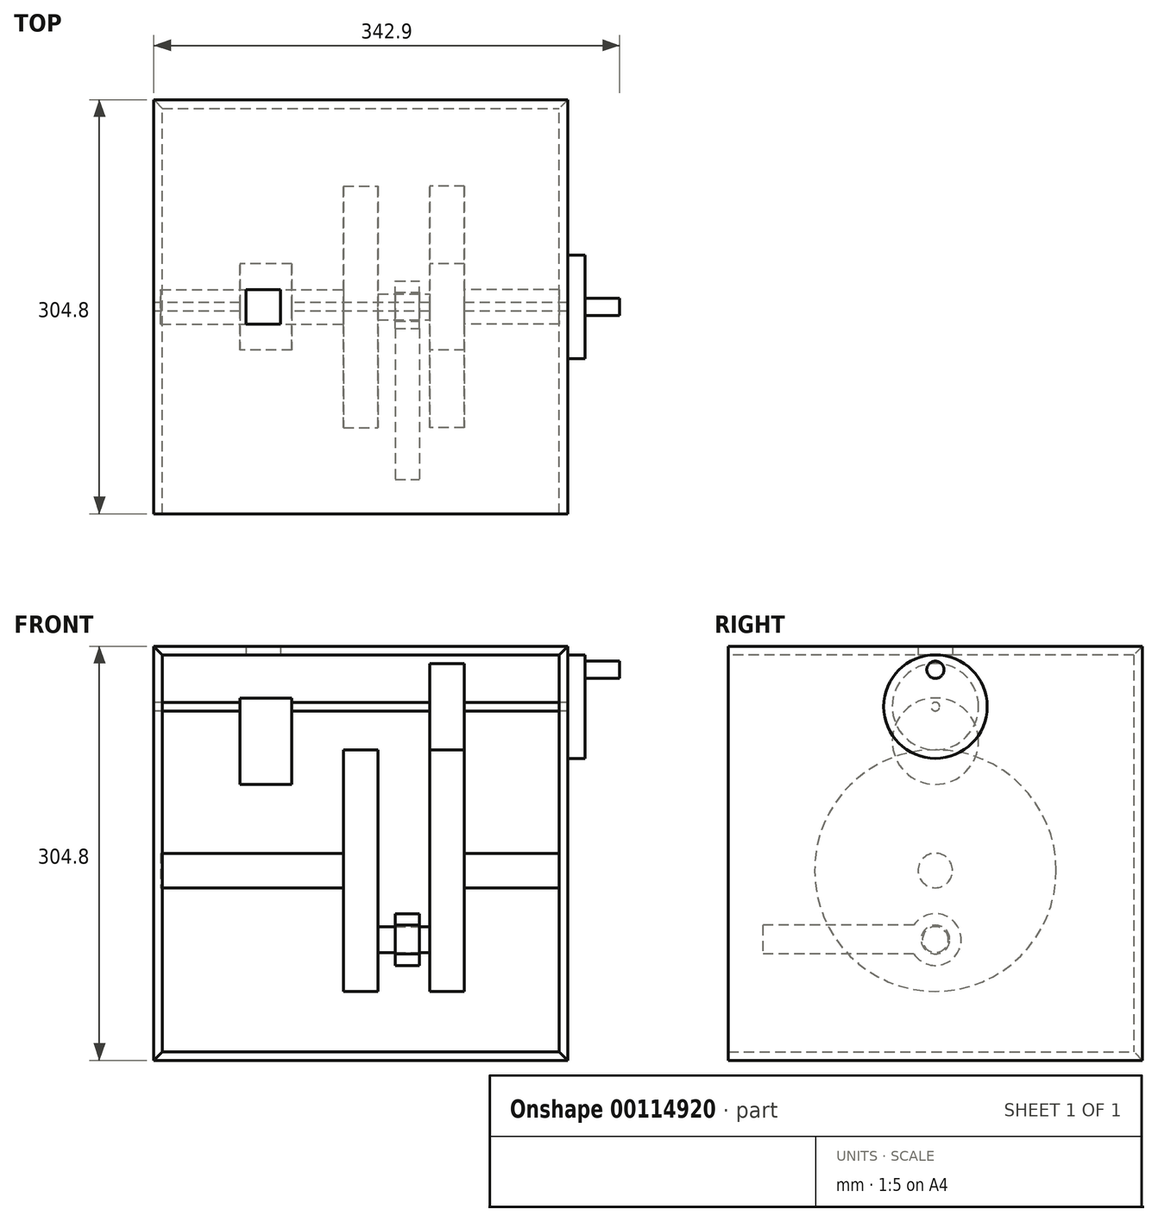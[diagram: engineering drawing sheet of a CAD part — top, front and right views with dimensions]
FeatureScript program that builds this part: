
annotation { "Feature Type Name" : "Feature", "Feature Type Description" : "" }
export const myFeature = defineFeature(function(context is Context, id is Id, definition is map)
    precondition{}
    {
        {
            var Q0;
            Q0=qCreatedBy(makeId("Right.planeOp"),FACE);
            var sketch = newSketch(context, id + "F0", { "sketchPlane" : qUnion([Q0])});
            skCircle(sketch, "E0", {"center": v(0, 0) * mm, "radius": 3.18 * mm});
            skSolve(sketch);
        }
        {
            var Q0;
            Q0=makeQuery(id+"F0.imprint","IMPRINT",FACE,{"disambiguationData":[TD([[makeQuery(id+"F0.imprint","IMPRINT",EDGE,{"derivedFrom":sQuery(id+"F0.wireOp",EDGE,"E0")}),1.0]])]});
            extrude(context, id + "F1", {"entities" : qUnion([Q0]), "depth" : 304.8 * mm});
        }
        {
            var Q0;
            Q0=qCreatedBy(makeId("Right.planeOp"),FACE);
            cPlane(context, id + "F2", {"entities" : qUnion([Q0]), "cplaneType" : CPlaneType.OFFSET, "offset" : 63.5 * mm, "width" : 152.4 * mm, "height" : 152.4 * mm});
        }
        {
            var Q0;
            Q0=qCreatedBy(id+"F2.planeOp",FACE);
            var sketch = newSketch(context, id + "F3", { "sketchPlane" : qUnion([Q0])});
            skCircle(sketch, "E1", {"center": v(0, -25.4) * mm, "radius": 31.75 * mm});
            skSolve(sketch);
        }
        {
            var Q0;
            Q0=makeQuery(id+"F3.imprint","IMPRINT",FACE,{"disambiguationData":[TD([[makeQuery(id+"F3.imprint","IMPRINT",EDGE,{"derivedFrom":sQuery(id+"F3.wireOp",EDGE,"E1")}),1.0]])]});
            extrude(context, id + "F4", {"entities" : qUnion([Q0]), "operationType" : NewBodyOperationType.ADD, "depth" : 38.1 * mm});
        }
        {
            var Q0;
            Q0=qCreatedBy(makeId("Top.planeOp"),FACE);
            cPlane(context, id + "F5", {"entities" : qUnion([Q0]), "cplaneType" : CPlaneType.OFFSET, "offset" : 38.1 * mm, "width" : 152.4 * mm, "height" : 152.4 * mm});
        }
        {
            var Q0;
            Q0=qCreatedBy(id+"F5.planeOp",FACE);
            var sketch = newSketch(context, id + "F6", { "sketchPlane" : qUnion([Q0])});
            skLineSegment(sketch, "E2.bottom", {"start": v(0, -152.4) * mm, "end": v(304.8, -152.4) * mm});
            skLineSegment(sketch, "E2.top", {"start": v(0, 152.4) * mm, "end": v(304.8, 152.4) * mm});
            skLineSegment(sketch, "E2.left", {"start": v(0, -152.4) * mm, "end": v(0, 152.4) * mm});
            skLineSegment(sketch, "E2.right", {"start": v(304.8, -152.4) * mm, "end": v(304.8, 152.4) * mm});
            skLineSegment(sketch, "E3.bottom", {"start": v(93.2, 12.7) * mm, "end": v(67.8, 12.7) * mm});
            skLineSegment(sketch, "E3.top", {"start": v(93.2, -12.7) * mm, "end": v(67.8, -12.7) * mm});
            skLineSegment(sketch, "E3.left", {"start": v(93.2, 12.7) * mm, "end": v(93.2, -12.7) * mm});
            skLineSegment(sketch, "E3.right", {"start": v(67.8, 12.7) * mm, "end": v(67.8, -12.7) * mm});
            skPoint(sketch, "E3.middle", {"position": v(80.5, 0) * mm});
            skSolve(sketch);
        }
        {
            var Q0;
            Q0=makeQuery(id+"F6.imprint","IMPRINT",FACE,{"disambiguationData":[TD([[makeQuery(id+"F6.imprint","IMPRINT",EDGE,{"derivedFrom":sQuery(id+"F6.wireOp",EDGE,"E2.bottom")}),1.0]])]});
            extrude(context, id + "F7", {"entities" : qUnion([Q0]), "depth" : 6.35 * mm});
        }
        {
            var Q0;
            Q0=makeQuery(id+"F7.opExtrude","CAP_EDGE",EDGE,{"disambiguationData":[OSD([sQuery(id+"F6.wireOp",EDGE,"E2.right")])],"isStart":true});
            var Q1;
            Q1=makeQuery(id+"F7.opExtrude","CAP_EDGE",EDGE,{"disambiguationData":[OSD([sQuery(id+"F6.wireOp",EDGE,"E2.top")])],"isStart":true});
            var Q2;
            Q2=makeQuery(id+"F7.opExtrude","CAP_EDGE",EDGE,{"disambiguationData":[OSD([sQuery(id+"F6.wireOp",EDGE,"E2.left")])],"isStart":true});
            chamfer(context, id + "F8", {"entities" : qUnion([Q0, Q1, Q2]), "width" : 6.35 * mm, "tangentPropagation" : true});
        }
        {
            var Q0;
            Q0=qCreatedBy(makeId("Right.planeOp"),FACE);
            var sketch = newSketch(context, id + "F9", { "sketchPlane" : qUnion([Q0])});
            skLineSegment(sketch, "E4.bottom", {"start": v(-152.4, -260.35) * mm, "end": v(152.4, -260.35) * mm});
            skLineSegment(sketch, "E4.top", {"start": v(-152.4, 44.45) * mm, "end": v(152.4, 44.45) * mm});
            skLineSegment(sketch, "E4.left", {"start": v(-152.4, -260.35) * mm, "end": v(-152.4, 44.45) * mm});
            skLineSegment(sketch, "E4.right", {"start": v(152.4, -260.35) * mm, "end": v(152.4, 44.45) * mm});
            skSolve(sketch);
        }
        {
            var Q0;
            Q0 = qSketchRegion(id + "F9", true);
            extrude(context, id + "F10", {"entities" : qUnion([Q0]), "depth" : 6.35 * mm});
        }
        {
            var Q0;
            Q0=makeQuery(id+"F10.opExtrude","CAP_EDGE",EDGE,{"disambiguationData":[OSD([sQuery(id+"F9.wireOp",EDGE,"E4.top")])],"isStart":false});
            var Q1;
            Q1=makeQuery(id+"F10.opExtrude","CAP_EDGE",EDGE,{"disambiguationData":[OSD([sQuery(id+"F9.wireOp",EDGE,"E4.bottom")])],"isStart":false});
            var Q2;
            Q2=makeQuery(id+"F10.opExtrude","CAP_EDGE",EDGE,{"disambiguationData":[OSD([sQuery(id+"F9.wireOp",EDGE,"E4.right")])],"isStart":false});
            chamfer(context, id + "F11", {"entities" : qUnion([Q0, Q1, Q2]), "width" : 6.35 * mm, "tangentPropagation" : true});
        }
        {
            var Q0;
            Q0=qCreatedBy(makeId("Front.planeOp"),FACE);
            cPlane(context, id + "F12", {"entities" : qUnion([Q0]), "cplaneType" : CPlaneType.OFFSET, "offset" : 152.4 * mm, "oppositeDirection" : true, "width" : 152.4 * mm, "height" : 152.4 * mm});
        }
        {
            var Q0;
            Q0=qCreatedBy(id+"F12.planeOp",FACE);
            var sketch = newSketch(context, id + "F13", { "sketchPlane" : qUnion([Q0])});
            skLineSegment(sketch, "E5.bottom", {"start": v(0, 44.45) * mm, "end": v(304.8, 44.45) * mm});
            skLineSegment(sketch, "E5.top", {"start": v(0, -260.35) * mm, "end": v(304.8, -260.35) * mm});
            skLineSegment(sketch, "E5.left", {"start": v(0, 44.45) * mm, "end": v(0, -260.35) * mm});
            skLineSegment(sketch, "E5.right", {"start": v(304.8, 44.45) * mm, "end": v(304.8, -260.35) * mm});
            skSolve(sketch);
        }
        {
            var Q0;
            Q0=makeQuery(id+"F13.imprint","IMPRINT",FACE,{"disambiguationData":[TD([[makeQuery(id+"F13.imprint","IMPRINT",EDGE,{"derivedFrom":sQuery(id+"F13.wireOp",EDGE,"E5.bottom")}),-1.0]])]});
            extrude(context, id + "F14", {"entities" : qUnion([Q0]), "depth" : 6.35 * mm});
        }
        {
            var Q0;
            Q0=makeQuery(id+"F14.opExtrude","CAP_EDGE",EDGE,{"disambiguationData":[OSD([sQuery(id+"F13.wireOp",EDGE,"E5.bottom")])],"isStart":false});
            var Q1;
            Q1=makeQuery(id+"F14.opExtrude","CAP_EDGE",EDGE,{"disambiguationData":[OSD([sQuery(id+"F13.wireOp",EDGE,"E5.right")])],"isStart":false});
            var Q2;
            Q2=makeQuery(id+"F14.opExtrude","CAP_EDGE",EDGE,{"disambiguationData":[OSD([sQuery(id+"F13.wireOp",EDGE,"E5.top")])],"isStart":false});
            var Q3;
            Q3=makeQuery(id+"F14.opExtrude","CAP_EDGE",EDGE,{"disambiguationData":[OSD([sQuery(id+"F13.wireOp",EDGE,"E5.left")])],"isStart":false});
            chamfer(context, id + "F15", {"entities" : qUnion([Q0, Q1, Q2, Q3]), "width" : 6.35 * mm, "tangentPropagation" : true});
        }
        {
            var Q0;
            Q0=makeQuery(id+"F7.opExtrude","CAP_FACE",FACE,{"disambiguationData":[OSD([sQuery(id+"F6.wireOp",EDGE,"E2.bottom"),sQuery(id+"F6.wireOp",EDGE,"E2.top"),sQuery(id+"F6.wireOp",EDGE,"E2.left"),sQuery(id+"F6.wireOp",EDGE,"E2.right"),sQuery(id+"F6.wireOp",EDGE,"E3.bottom"),sQuery(id+"F6.wireOp",EDGE,"E3.top"),sQuery(id+"F6.wireOp",EDGE,"E3.left"),sQuery(id+"F6.wireOp",EDGE,"E3.right")])],"isStart":false});
            cPlane(context, id + "F16", {"entities" : qUnion([Q0]), "cplaneType" : CPlaneType.OFFSET, "offset" : 304.8 * mm, "oppositeDirection" : true, "width" : 152.4 * mm, "height" : 152.4 * mm});
        }
        {
            var Q0;
            Q0=qCreatedBy(id+"F16.planeOp",FACE);
            var sketch = newSketch(context, id + "F17", { "sketchPlane" : qUnion([Q0])});
            skLineSegment(sketch, "E6.bottom", {"start": v(0, 152.4) * mm, "end": v(304.8, 152.4) * mm});
            skLineSegment(sketch, "E6.top", {"start": v(0, -152.4) * mm, "end": v(304.8, -152.4) * mm});
            skLineSegment(sketch, "E6.left", {"start": v(0, 152.4) * mm, "end": v(0, -152.4) * mm});
            skLineSegment(sketch, "E6.right", {"start": v(304.8, 152.4) * mm, "end": v(304.8, -152.4) * mm});
            skSolve(sketch);
        }
        {
            var Q0;
            Q0=makeQuery(id+"F17.imprint","IMPRINT",FACE,{"disambiguationData":[TD([[makeQuery(id+"F17.imprint","IMPRINT",EDGE,{"derivedFrom":sQuery(id+"F17.wireOp",EDGE,"E6.bottom")}),-1.0]])]});
            extrude(context, id + "F18", {"entities" : qUnion([Q0]), "depth" : 6.35 * mm});
        }
        {
            var Q0;
            Q0=makeQuery(id+"F18.opExtrude","CAP_EDGE",EDGE,{"disambiguationData":[OSD([sQuery(id+"F17.wireOp",EDGE,"E6.left")])],"isStart":false});
            var Q1;
            Q1=makeQuery(id+"F18.opExtrude","CAP_EDGE",EDGE,{"disambiguationData":[OSD([sQuery(id+"F17.wireOp",EDGE,"E6.bottom")])],"isStart":false});
            var Q2;
            Q2=makeQuery(id+"F18.opExtrude","CAP_EDGE",EDGE,{"disambiguationData":[OSD([sQuery(id+"F17.wireOp",EDGE,"E6.right")])],"isStart":false});
            chamfer(context, id + "F19", {"entities" : qUnion([Q0, Q1, Q2]), "width" : 6.35 * mm, "tangentPropagation" : true});
        }
        {
            var Q0;
            Q0=qCreatedBy(makeId("Right.planeOp"),FACE);
            cPlane(context, id + "F20", {"entities" : qUnion([Q0]), "cplaneType" : CPlaneType.OFFSET, "offset" : 203.2 * mm, "width" : 152.4 * mm, "height" : 152.4 * mm});
        }
        {
            var Q0;
            Q0=qCreatedBy(id+"F20.planeOp",FACE);
            var sketch = newSketch(context, id + "F21", { "sketchPlane" : qUnion([Q0])});
            skCircle(sketch, "E7", {"center": v(0, 0) * mm, "radius": 31.75 * mm});
            skCircle(sketch, "E8", {"center": v(0, -120.65) * mm, "radius": 88.9 * mm});
            skSolve(sketch);
        }
        {
            var Q0;
            Q0=makeQuery(id+"F21.imprint","IMPRINT",FACE,{"disambiguationData":[TD([[makeQuery(id+"F21.imprint","IMPRINT",EDGE,{"derivedFrom":sQuery(id+"F21.wireOp",EDGE,"E8")}),1.0]])]});
            var Q1;
            Q1=makeQuery(id+"F21.imprint","IMPRINT",FACE,{"disambiguationData":[TD([[makeQuery(id+"F21.imprint","IMPRINT",EDGE,{"derivedFrom":sQuery(id+"F21.wireOp",EDGE,"E7")}),1.0]])]});
            extrude(context, id + "F22", {"entities" : qUnion([Q0, Q1]), "operationType" : NewBodyOperationType.ADD, "depth" : 25.4 * mm});
        }
        {
            var Q0;
            Q0=makeQuery(id+"F22.opExtrude","CAP_FACE",FACE,{"disambiguationData":[OSD([sQuery(id+"F21.wireOp",EDGE,"E8")])],"isStart":true});
            var sketch = newSketch(context, id + "F23", { "sketchPlane" : qUnion([Q0])});
            skCircle(sketch, "E9", {"center": v(0, -171.45) * mm, "radius": 9.53 * mm});
            skSolve(sketch);
        }
        {
            var Q0;
            Q0=makeQuery(id+"F23.imprint","IMPRINT",FACE,{"disambiguationData":[TD([[makeQuery(id+"F23.imprint","IMPRINT",EDGE,{"derivedFrom":sQuery(id+"F23.wireOp",EDGE,"E9")}),1.0]])]});
            var Q1;
            Q1=sQuery(id+"F23.wireOp",EDGE,"E9");
            extrude(context, id + "F24", {"entities" : qUnion([Q0]), "surfaceEntities" : qUnion([Q1]), "depth" : 38.1 * mm});
        }
        {
            var Q0;
            Q0=qCreatedBy(makeId("Right.planeOp"),FACE);
            cPlane(context, id + "F25", {"entities" : qUnion([Q0]), "cplaneType" : CPlaneType.OFFSET, "offset" : 304.8 * mm, "width" : 152.4 * mm, "height" : 152.4 * mm});
        }
        {
            var Q0;
            Q0=qCreatedBy(id+"F25.planeOp",FACE);
            var sketch = newSketch(context, id + "F26", { "sketchPlane" : qUnion([Q0])});
            skLineSegment(sketch, "E10.bottom", {"start": v(152.4, 44.45) * mm, "end": v(-152.4, 44.45) * mm});
            skLineSegment(sketch, "E10.top", {"start": v(152.4, -260.35) * mm, "end": v(-152.4, -260.35) * mm});
            skLineSegment(sketch, "E10.left", {"start": v(152.4, 44.45) * mm, "end": v(152.4, -260.35) * mm});
            skLineSegment(sketch, "E10.right", {"start": v(-152.4, 44.45) * mm, "end": v(-152.4, -260.35) * mm});
            skSolve(sketch);
        }
        {
            var Q0;
            Q0=makeQuery(id+"F26.imprint","IMPRINT",FACE,{"disambiguationData":[TD([[makeQuery(id+"F26.imprint","IMPRINT",EDGE,{"derivedFrom":sQuery(id+"F26.wireOp",EDGE,"E10.bottom")}),1.0]])]});
            extrude(context, id + "F27", {"entities" : qUnion([Q0]), "oppositeDirection" : true, "depth" : 6.35 * mm});
        }
        {
            var Q0;
            Q0=makeQuery(id+"F27.opExtrude","CAP_EDGE",EDGE,{"disambiguationData":[OSD([sQuery(id+"F26.wireOp",EDGE,"E10.bottom")])],"isStart":false});
            var Q1;
            Q1=makeQuery(id+"F27.opExtrude","CAP_EDGE",EDGE,{"disambiguationData":[OSD([sQuery(id+"F26.wireOp",EDGE,"E10.left")])],"isStart":false});
            var Q2;
            Q2=makeQuery(id+"F27.opExtrude","CAP_EDGE",EDGE,{"disambiguationData":[OSD([sQuery(id+"F26.wireOp",EDGE,"E10.top")])],"isStart":false});
            chamfer(context, id + "F28", {"entities" : qUnion([Q0, Q1, Q2]), "width" : 6.35 * mm, "tangentPropagation" : true});
        }
        {
            var Q0;
            Q0=makeQuery(id+"F27.opExtrude","CAP_FACE",FACE,{"disambiguationData":[OSD([sQuery(id+"F26.wireOp",EDGE,"E10.bottom"),sQuery(id+"F26.wireOp",EDGE,"E10.top"),sQuery(id+"F26.wireOp",EDGE,"E10.left"),sQuery(id+"F26.wireOp",EDGE,"E10.right")])],"isStart":true});
            var sketch = newSketch(context, id + "F29", { "sketchPlane" : qUnion([Q0])});
            skCircle(sketch, "E11", {"center": v(0, 0) * mm, "radius": 38.1 * mm});
            skSolve(sketch);
        }
        {
            var Q0;
            Q0 = qSketchRegion(id + "F29", true);
            extrude(context, id + "F30", {"entities" : qUnion([Q0]), "depth" : 12.7 * mm});
        }
        {
            var Q0;
            Q0=makeQuery(id+"F30.opExtrude","CAP_FACE",FACE,{"disambiguationData":[OSD([sQuery(id+"F29.wireOp",EDGE,"E11")])],"isStart":false});
            var sketch = newSketch(context, id + "F31", { "sketchPlane" : qUnion([Q0])});
            skCircle(sketch, "E12", {"center": v(0, 27.1) * mm, "radius": 6.35 * mm});
            skSolve(sketch);
        }
        {
            var Q0;
            Q0=makeQuery(id+"F31.imprint","IMPRINT",FACE,{"disambiguationData":[TD([[makeQuery(id+"F31.imprint","IMPRINT",EDGE,{"derivedFrom":sQuery(id+"F31.wireOp",EDGE,"E12")}),1.0]])]});
            extrude(context, id + "F32", {"entities" : qUnion([Q0]), "operationType" : NewBodyOperationType.ADD, "depth" : 25.4 * mm});
        }
        {
            var Q0;
            Q0=makeQuery(id+"F22.opExtrude","CAP_FACE",FACE,{"disambiguationData":[OSD([sQuery(id+"F21.wireOp",EDGE,"E8")])],"isStart":false});
            var sketch = newSketch(context, id + "F33", { "sketchPlane" : qUnion([Q0])});
            skCircle(sketch, "E13", {"center": v(0, -120.65) * mm, "radius": 12.7 * mm});
            skSolve(sketch);
        }
        {
            var Q0;
            Q0=makeQuery(id+"F33.imprint","IMPRINT",FACE,{"disambiguationData":[TD([[makeQuery(id+"F33.imprint","IMPRINT",EDGE,{"derivedFrom":sQuery(id+"F33.wireOp",EDGE,"E13")}),1.0]])]});
            var Q1;
            Q1=sQuery(id+"F33.wireOp",EDGE,"E13");
            extrude(context, id + "F34", {"entities" : qUnion([Q0]), "surfaceEntities" : qUnion([Q1]), "depth" : 69.85 * mm});
        }
        {
            var Q0;
            Q0=makeQuery(id+"F22.opExtrude","CAP_FACE",FACE,{"disambiguationData":[OSD([sQuery(id+"F21.wireOp",EDGE,"E8")])],"isStart":true});
            cPlane(context, id + "F35", {"entities" : qUnion([Q0]), "cplaneType" : CPlaneType.OFFSET, "offset" : 38.1 * mm, "width" : 152.4 * mm, "height" : 152.4 * mm});
        }
        {
            var Q0;
            Q0=qCreatedBy(id+"F35.planeOp",FACE);
            var sketch = newSketch(context, id + "F36", { "sketchPlane" : qUnion([Q0])});
            skCircle(sketch, "E14", {"center": v(0, -120.65) * mm, "radius": 88.9 * mm});
            skSolve(sketch);
        }
        {
            var Q0;
            Q0=makeQuery(id+"F36.imprint","IMPRINT",FACE,{"disambiguationData":[TD([[makeQuery(id+"F36.imprint","IMPRINT",EDGE,{"derivedFrom":sQuery(id+"F36.wireOp",EDGE,"E14")}),1.0]])]});
            extrude(context, id + "F37", {"entities" : qUnion([Q0]), "operationType" : NewBodyOperationType.ADD, "depth" : 25.4 * mm});
        }
        {
            var Q0;
            Q0=makeQuery(id+"F37.opExtrude","CAP_FACE",FACE,{"disambiguationData":[OSD([sQuery(id+"F36.wireOp",EDGE,"E14")])],"isStart":false});
            var sketch = newSketch(context, id + "F38", { "sketchPlane" : qUnion([Q0])});
            skCircle(sketch, "E15", {"center": v(0, -120.65) * mm, "radius": 12.7 * mm});
            skSolve(sketch);
        }
        {
            var Q0;
            Q0=makeQuery(id+"F38.imprint","IMPRINT",FACE,{"disambiguationData":[TD([[makeQuery(id+"F38.imprint","IMPRINT",EDGE,{"derivedFrom":sQuery(id+"F38.wireOp",EDGE,"E15")}),1.0]])]});
            var Q1;
            Q1=sQuery(id+"F38.wireOp",EDGE,"E15");
            extrude(context, id + "F39", {"entities" : qUnion([Q0]), "surfaceEntities" : qUnion([Q1]), "depth" : 134.62 * mm});
        }
        {
            var Q0;
            Q0=makeQuery(id+"F24.opExtrude","CAP_FACE",FACE,{"disambiguationData":[OSD([sQuery(id+"F23.wireOp",EDGE,"E9")])],"isStart":true});
            var sketch = newSketch(context, id + "F40", { "sketchPlane" : qUnion([Q0])});
            skCircle(sketch, "E16", {"center": v(0, -171.45) * mm, "radius": 19.05 * mm});
            skCircle(sketch, "E17", {"center": v(0, -171.45) * mm, "radius": 10.54 * mm});
            skLineSegment(sketch, "E18.bottom", {"start": v(0, -160.9) * mm, "end": v(-127, -160.9) * mm});
            skLineSegment(sketch, "E18.top", {"start": v(0, -182) * mm, "end": v(-127, -182) * mm});
            skLineSegment(sketch, "E18.left", {"start": v(0, -160.9) * mm, "end": v(0, -182) * mm});
            skLineSegment(sketch, "E18.right", {"start": v(-127, -160.9) * mm, "end": v(-127, -182) * mm});
            skSolve(sketch);
        }
        {
            var Q0;
            {var subQ5=sQuery(id+"F40.wireOp",EDGE,"E18.right");Q0=makeQuery(id+"F40.imprint","IMPRINT",FACE,{"disambiguationData":[TD([[makeQuery(id+"F40.imprint","IMPRINT",EDGE,{"derivedFrom":subQ5}),1.0]])]});}
            var Q1;
            {var subQ0=sQuery(id+"F40.wireOp",EDGE,"E18.bottom");var subQ1=sQuery(id+"F40.wireOp",EDGE,"E16");var subQ2=makeQuery(id+"F40.imprint","INTERSECT",VERTEX,{"derivedFrom":[subQ1,subQ0]});Q1=makeQuery(id+"F40.imprint","IMPRINT",FACE,{"disambiguationData":[TD([[makeQuery(id+"F40.imprint","IMPRINT",EDGE,{"disambiguationData":[TD([[subQ2,-1.0]])],"derivedFrom":subQ1}),1.0]])]});}
            var Q2;
            {var subQ0=sQuery(id+"F40.wireOp",EDGE,"E18.bottom");var subQ1=sQuery(id+"F40.wireOp",EDGE,"E16");var subQ2=makeQuery(id+"F40.imprint","INTERSECT",VERTEX,{"derivedFrom":[subQ1,subQ0]});Q2=makeQuery(id+"F40.imprint","IMPRINT",FACE,{"disambiguationData":[TD([[makeQuery(id+"F40.imprint","IMPRINT",EDGE,{"disambiguationData":[TD([[subQ2,1.0]])],"derivedFrom":subQ1}),1.0]])]});}
            extrude(context, id + "F41", {"entities" : qUnion([Q0, Q1, Q2]), "oppositeDirection" : true, "depth" : 25.4 * mm});
        }
        {
            var Q0;
            Q0=makeQuery(id+"F41.opExtrude","CAP_FACE",FACE,{"disambiguationData":[OSD([sQuery(id+"F40.wireOp",EDGE,"E16"),sQuery(id+"F40.wireOp",EDGE,"E17"),sQuery(id+"F40.wireOp",EDGE,"E18.bottom"),sQuery(id+"F40.wireOp",EDGE,"E18.top"),sQuery(id+"F40.wireOp",EDGE,"E18.right")])],"isStart":true});
            extrude(context, id + "F42", {"entities" : qUnion([Q0]), "operationType" : NewBodyOperationType.REMOVE, "oppositeDirection" : true, "depth" : 7.62 * mm});
        }
    });
